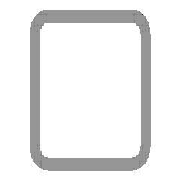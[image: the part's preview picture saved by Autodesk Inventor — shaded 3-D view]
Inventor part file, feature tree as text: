
AUTODESK INVENTOR PART (.ipt)
format: ipt  version: 2025 (Build 290162010, 162A)  size: 134,144 bytes
history: native  units: mm (DEFAULTED — no unit token found)
features: other x4, sketch x1, plane x1
ambient origin geometry x8: Origin, YZ Plane, XZ Plane, XY Plane, X Axis, Y Axis, Z Axis, Center Point
bodies: Solid1 (feature_tree), Body (feature_tree)
feature tree (6):
  parser-record x1  (decoder bookkeeping rows leaked as tree rows — omitted from the tree; the rows remain in map.json)
  other  "Driven Length"
  other  "Start Plane"
  other  "End Plane"
  sketch  "Sketch3"  dims[d3=1400.0mm d4=0.0mm d7=8.0mm d9=100.0mm d11=100.0mm d12=4.0mm d13=50.0mm d14=1450.0mm d15=50.0mm d16=50.0mm d17=90.0deg d18=1400.0mm]
  plane  "Work Plane3"
